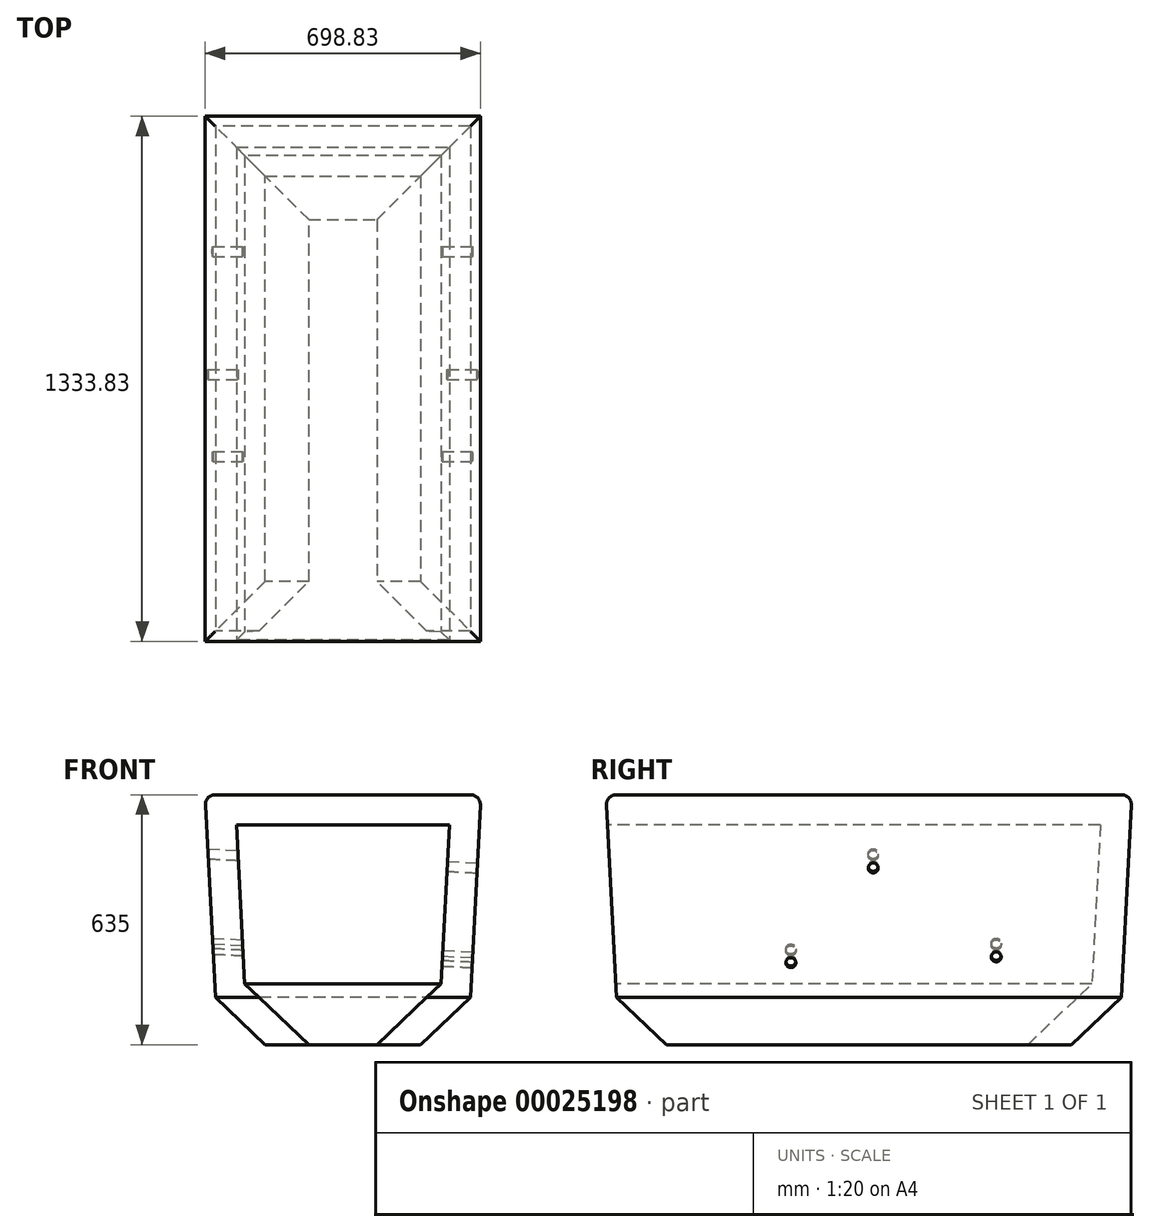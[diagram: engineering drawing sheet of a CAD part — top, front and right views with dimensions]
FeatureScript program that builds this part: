
annotation { "Feature Type Name" : "Feature", "Feature Type Description" : "" }
export const myFeature = defineFeature(function(context is Context, id is Id, definition is map)
    precondition{}
    {
        {
            var Q0;
            Q0=qCreatedBy(makeId("Top.planeOp"),FACE);
            var sketch = newSketch(context, id + "F0", { "sketchPlane" : qUnion([Q0])});
            skLineSegment(sketch, "E0.bottom", {"start": v(-460.95, -599.89) * mm, "end": v(174.05, -599.89) * mm});
            skLineSegment(sketch, "E0.top", {"start": v(-460.95, 670.11) * mm, "end": v(174.05, 670.11) * mm});
            skLineSegment(sketch, "E0.left", {"start": v(-460.95, -599.89) * mm, "end": v(-460.95, 670.11) * mm});
            skLineSegment(sketch, "E0.right", {"start": v(174.05, -599.89) * mm, "end": v(174.05, 670.11) * mm});
            skSolve(sketch);
        }
        {
            var Q0;
            Q0=makeQuery(id+"F0.imprint","IMPRINT",FACE,{"disambiguationData":[TD([[makeQuery(id+"F0.imprint","IMPRINT",EDGE,{"derivedFrom":sQuery(id+"F0.wireOp",EDGE,"E0.bottom")}),1.0]])]});
            extrude(context, id + "F1", {"entities" : qUnion([Q0]), "depth" : 635 * mm, "hasDraft" : true, "draftAngle" : 3 * degree});
        }
        {
            var Q0;
            Q0=makeQuery(id+"F1.opExtrude","CAP_EDGE",EDGE,{"disambiguationData":[OSD([sQuery(id+"F0.wireOp",EDGE,"E0.bottom")])],"isStart":false});
            var Q1;
            Q1=makeQuery(id+"F1.opExtrude","CAP_EDGE",EDGE,{"disambiguationData":[OSD([sQuery(id+"F0.wireOp",EDGE,"E0.right")])],"isStart":false});
            var Q2;
            Q2=makeQuery(id+"F1.opExtrude","CAP_EDGE",EDGE,{"disambiguationData":[OSD([sQuery(id+"F0.wireOp",EDGE,"E0.top")])],"isStart":false});
            var Q3;
            Q3=makeQuery(id+"F1.opExtrude","CAP_EDGE",EDGE,{"disambiguationData":[OSD([sQuery(id+"F0.wireOp",EDGE,"E0.left")])],"isStart":false});
            fillet(context, id + "F2", {"entities" : qUnion([Q0, Q1, Q2, Q3]), "radius" : 25.4 * mm, "tangentPropagation" : true, "allowEdgeOverflow" : false});
        }
        {
            var Q0;
            Q0=makeQuery(id+"F1.opExtrude","CAP_FACE",FACE,{"disambiguationData":[OSD([sQuery(id+"F0.wireOp",EDGE,"E0.bottom"),sQuery(id+"F0.wireOp",EDGE,"E0.top"),sQuery(id+"F0.wireOp",EDGE,"E0.left"),sQuery(id+"F0.wireOp",EDGE,"E0.right")])],"isStart":true});
            chamfer(context, id + "F3", {"entities" : qUnion([Q0]), "width" : 127 * mm, "tangentPropagation" : true});
        }
        {
            var Q0;
            Q0=makeQuery(id+"F1.opExtrude","SWEPT_FACE",FACE,{"disambiguationData":[OSD([sQuery(id+"F0.wireOp",EDGE,"E0.bottom")])]});
            var Q1;
            Q1=makeQuery(id+"F3.opChamfer","BLEND_FACE",FACE,{"disambiguationData":[OSD([sQuery(id+"F0.wireOp",EDGE,"E0.bottom")])]});
            var Q2;
            Q2=makeQuery(id+"F1.opExtrude","CAP_FACE",FACE,{"disambiguationData":[OSD([sQuery(id+"F0.wireOp",EDGE,"E0.bottom"),sQuery(id+"F0.wireOp",EDGE,"E0.top"),sQuery(id+"F0.wireOp",EDGE,"E0.left"),sQuery(id+"F0.wireOp",EDGE,"E0.right")])],"isStart":true});
            shell(context, id + "F4", {"entities" : qUnion([Q0, Q1, Q2]), "thickness" : 76.2 * mm});
        }
        {
            var Q0;
            Q0=makeQuery(id+"F1.opExtrude","SWEPT_FACE",FACE,{"disambiguationData":[OSD([sQuery(id+"F0.wireOp",EDGE,"E0.right")])]});
            var sketch = newSketch(context, id + "F5", { "sketchPlane" : qUnion([Q0])});
            skPoint(sketch, "E1", {"position": v(358.6, 232.63) * mm});
            skPoint(sketch, "E2", {"position": v(-163.05, 217.82) * mm});
            skPoint(sketch, "E3", {"position": v(46.13, 458.9) * mm});
            skSolve(sketch);
        }
        {
            var Q0;
            Q0=sQuery(id+"F5.wireOp",VERTEX,"E1");
            var Q1;
            Q1=sQuery(id+"F5.wireOp",VERTEX,"E3");
            var Q2;
            Q2=sQuery(id+"F5.wireOp",VERTEX,"E2");
            var Q3;
            Q3=makeQuery(id+"F1.opExtrude","SWEPT_BODY",BODY,{"disambiguationData":[OSD([sQuery(id+"F0.wireOp",EDGE,"E0.bottom"),sQuery(id+"F0.wireOp",EDGE,"E0.top"),sQuery(id+"F0.wireOp",EDGE,"E0.left"),sQuery(id+"F0.wireOp",EDGE,"E0.right")])]});
            hole(context, id + "F6", {"style" : HoleStyle.SIMPLE, "holeDiameter" : 25.4 * mm, "endStyle" : HoleEndStyle.THROUGH, "locations" : qUnion([Q0, Q1, Q2]), "scope" : qUnion([Q3])});
        }
    });
